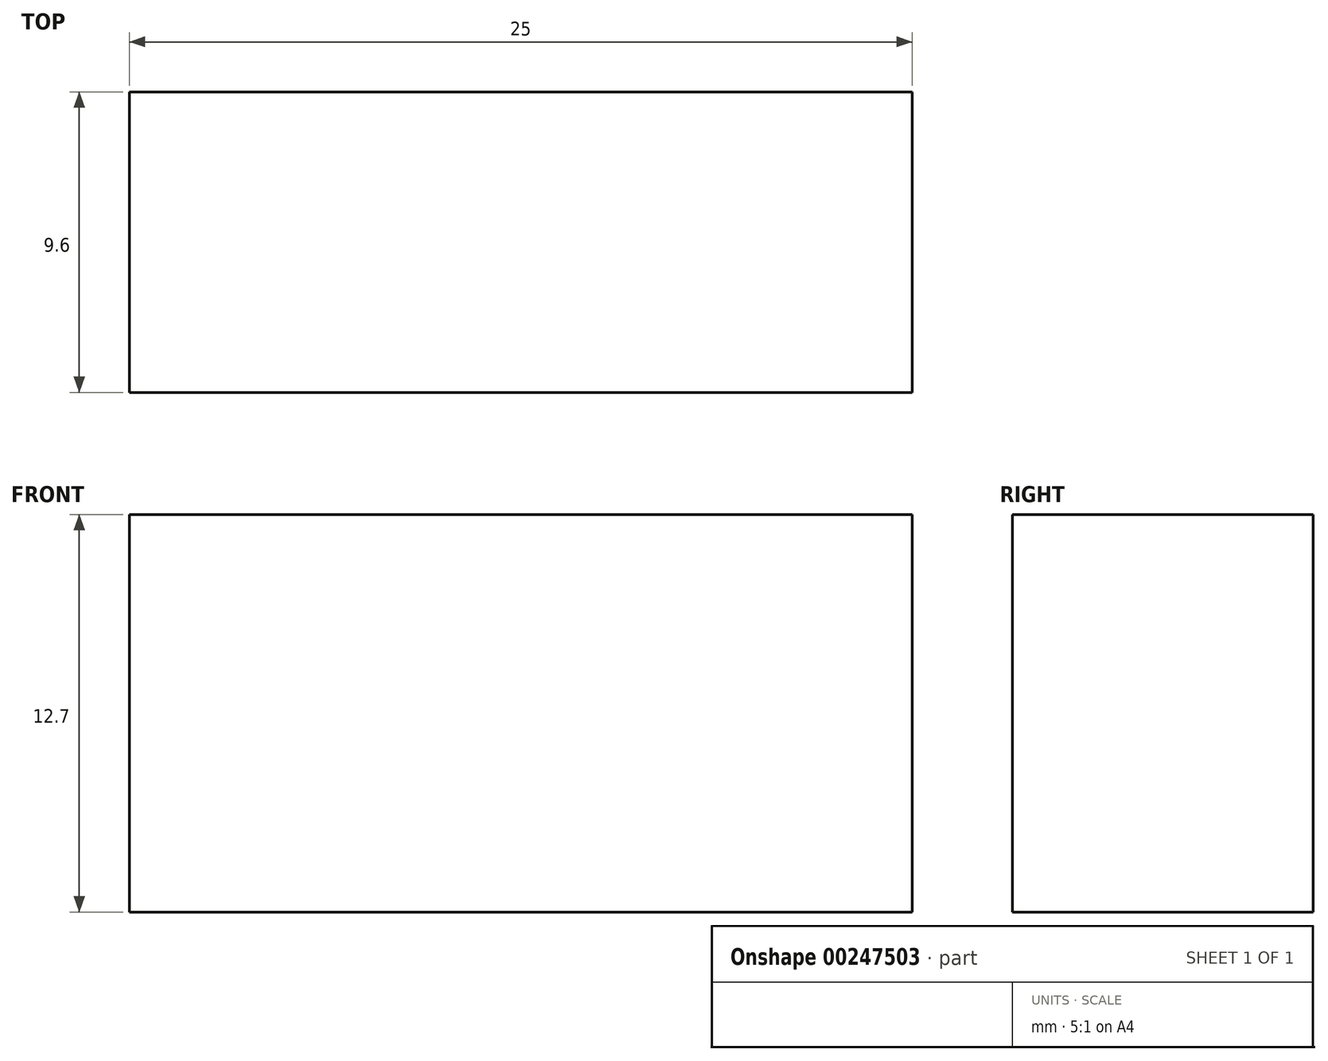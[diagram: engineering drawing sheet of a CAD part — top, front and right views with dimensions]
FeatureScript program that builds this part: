
annotation { "Feature Type Name" : "Feature", "Feature Type Description" : "" }
export const myFeature = defineFeature(function(context is Context, id is Id, definition is map)
    precondition{}
    {
        {
            var Q0;
            Q0=qCreatedBy(makeId("Top.planeOp"),FACE);
            var sketch = newSketch(context, id + "F0", { "sketchPlane" : qUnion([Q0])});
            skLineSegment(sketch, "E0.bottom", {"start": v(12.5, -4.8) * mm, "end": v(-12.5, -4.8) * mm});
            skLineSegment(sketch, "E0.top", {"start": v(12.5, 4.8) * mm, "end": v(-12.5, 4.8) * mm});
            skLineSegment(sketch, "E0.left", {"start": v(12.5, -4.8) * mm, "end": v(12.5, 4.8) * mm});
            skLineSegment(sketch, "E0.right", {"start": v(-12.5, -4.8) * mm, "end": v(-12.5, 4.8) * mm});
            skPoint(sketch, "E0.middle", {"position": v(0, 0) * mm});
            skSolve(sketch);
        }
        {
            var Q0;
            Q0=qSketchRegion(id+"F0",true);
            extrude(context, id + "F1", {"entities" : qUnion([Q0]), "depth" : 12.7 * mm});
        }
    });
